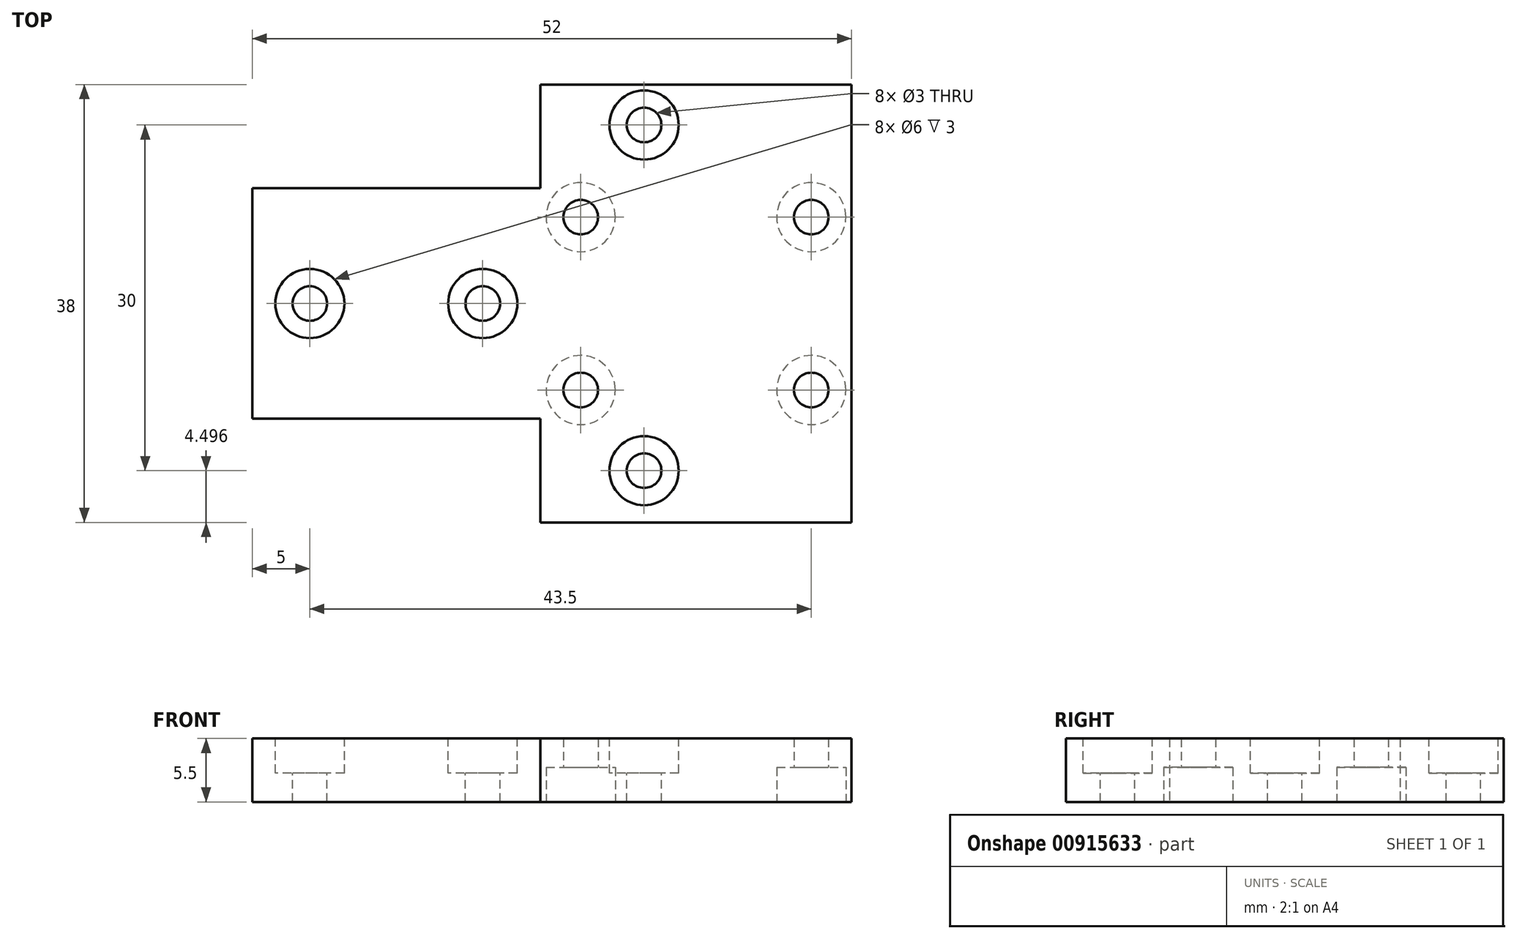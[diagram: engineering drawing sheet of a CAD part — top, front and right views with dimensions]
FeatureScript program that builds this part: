
annotation { "Feature Type Name" : "Feature", "Feature Type Description" : "" }
export const myFeature = defineFeature(function(context is Context, id is Id, definition is map)
    precondition{}
    {
        {
            var Q0;
            Q0=qCreatedBy(makeId("Top.planeOp"),FACE);
            var sketch = newSketch(context, id + "F0", { "sketchPlane" : qUnion([Q0])});
            skLineSegment(sketch, "E0.bottom", {"start": v(13.5, -19) * mm, "end": v(-13.5, -19) * mm});
            skLineSegment(sketch, "E0.top", {"start": v(13.5, 19) * mm, "end": v(-13.5, 19) * mm});
            skLineSegment(sketch, "E0.left", {"start": v(13.5, -19) * mm, "end": v(13.5, 19) * mm});
            skLineSegment(sketch, "E0.right", {"start": v(-13.5, -19) * mm, "end": v(-13.5, 19) * mm});
            skPoint(sketch, "E0.middle", {"position": v(0, 0) * mm});
            skLineSegment(sketch, "E1.bottom", {"start": v(10, -7.5) * mm, "end": v(-10, -7.5) * mm});
            skLineSegment(sketch, "E1.top", {"start": v(10, 7.5) * mm, "end": v(-10, 7.5) * mm});
            skLineSegment(sketch, "E1.left", {"start": v(10, -7.5) * mm, "end": v(10, 7.5) * mm});
            skLineSegment(sketch, "E1.right", {"start": v(-10, -7.5) * mm, "end": v(-10, 7.5) * mm});
            skSolve(sketch);
        }
        {
            var Q0;
            Q0=makeQuery(id+"F0.imprint","IMPRINT",FACE,{"disambiguationData":[TD([[makeQuery(id+"F0.imprint","IMPRINT",EDGE,{"derivedFrom":sQuery(id+"F0.wireOp",EDGE,"E0.bottom")}),-1.0]])]});
            var Q1;
            Q1=makeQuery(id+"F0.imprint","IMPRINT",FACE,{"disambiguationData":[TD([[makeQuery(id+"F0.imprint","IMPRINT",EDGE,{"derivedFrom":sQuery(id+"F0.wireOp",EDGE,"E1.bottom")}),-1.0]])]});
            extrude(context, id + "F1", {"entities" : qUnion([Q0, Q1]), "depth" : 5.5 * mm, "offsetDistance" : 25 * mm});
        }
        {
            var Q0;
            Q0=sQuery(id+"F0.wireOp",VERTEX,"E1.bottom.end");
            var Q1;
            Q1=sQuery(id+"F0.wireOp",VERTEX,"E1.top.end");
            var Q2;
            Q2=sQuery(id+"F0.wireOp",VERTEX,"E1.bottom.start");
            var Q3;
            Q3=sQuery(id+"F0.wireOp",VERTEX,"E1.top.start");
            var Q4;
            Q4=makeQuery(id+"F1.opExtrude","SWEPT_BODY",BODY,{"disambiguationData":[OSD([sQuery(id+"F0.wireOp",EDGE,"E0.bottom"),sQuery(id+"F0.wireOp",EDGE,"E0.top"),sQuery(id+"F0.wireOp",EDGE,"E0.left"),sQuery(id+"F0.wireOp",EDGE,"E0.right")])]});
            hole(context, id + "F2", {"style" : HoleStyle.C_BORE, "endStyle" : HoleEndStyle.BLIND, "oppositeDirection" : true, "holeDiameter" : 3 * mm, "cBoreDiameter" : 6 * mm, "cBoreDepth" : 3 * mm, "majorDiameter" : 5 * mm, "holeDepth" : 50 * mm, "isTappedThrough" : true, "tappedDepth" : 12 * mm, "tapClearance" : 3, "locations" : qUnion([Q0, Q1, Q2, Q3]), "scope" : qUnion([Q4])});
        }
        {
            var Q0;
            Q0=makeQuery(id+"F1.opExtrude","CAP_FACE",FACE,{"disambiguationData":[OSD([sQuery(id+"F0.wireOp",EDGE,"E0.bottom"),sQuery(id+"F0.wireOp",EDGE,"E0.top"),sQuery(id+"F0.wireOp",EDGE,"E0.left"),sQuery(id+"F0.wireOp",EDGE,"E0.right")])],"isStart":false});
            var sketch = newSketch(context, id + "F3", { "sketchPlane" : qUnion([Q0])});
            skLineSegment(sketch, "E2.bottom", {"start": v(-4.5, -14.5) * mm, "end": v(-13.5, -14.5) * mm});
            skLineSegment(sketch, "E2.top", {"start": v(-4.5, 15.5) * mm, "end": v(-13.5, 15.5) * mm});
            skLineSegment(sketch, "E2.left", {"start": v(-4.5, -14.5) * mm, "end": v(-4.5, 15.5) * mm});
            skLineSegment(sketch, "E2.right", {"start": v(-13.5, -14.5) * mm, "end": v(-13.5, 15.5) * mm});
            skPoint(sketch, "E2.middle", {"position": v(0, 0.5) * mm});
            skCircle(sketch, "E3", {"center": v(-4.5, -14.5) * mm, "radius": 7 * mm});
            skCircle(sketch, "E4", {"center": v(-4.5, 15.5) * mm, "radius": 7 * mm});
            skLineSegment(sketch, "E5", {"start": v(-13.5, 0) * mm, "end": v(-13.5, 10) * mm});
            skLineSegment(sketch, "E6", {"start": v(-13.5, 0) * mm, "end": v(-13.5, -10) * mm});
            skSolve(sketch);
        }
        {
            var Q0;
            Q0=sQuery(id+"F3.wireOp",VERTEX,"E2.bottom.start");
            var Q1;
            Q1=sQuery(id+"F3.wireOp",VERTEX,"E2.top.start");
            var Q2;
            Q2=makeQuery(id+"F1.opExtrude","SWEPT_BODY",BODY,{"disambiguationData":[OSD([sQuery(id+"F0.wireOp",EDGE,"E0.bottom"),sQuery(id+"F0.wireOp",EDGE,"E0.top"),sQuery(id+"F0.wireOp",EDGE,"E0.left"),sQuery(id+"F0.wireOp",EDGE,"E0.right")])]});
            hole(context, id + "F4", {"style" : HoleStyle.C_BORE, "endStyle" : HoleEndStyle.BLIND, "holeDiameter" : 3 * mm, "cBoreDiameter" : 6 * mm, "cBoreDepth" : 3 * mm, "majorDiameter" : 5 * mm, "holeDepth" : 50 * mm, "isTappedThrough" : true, "tappedDepth" : 12 * mm, "tapClearance" : 3, "locations" : qUnion([Q0, Q1]), "scope" : qUnion([Q2])});
        }
        {
            var Q0;
            Q0=makeQuery(id+"F1.opExtrude","SWEPT_FACE",FACE,{"disambiguationData":[OSD([sQuery(id+"F0.wireOp",EDGE,"E0.right")])]});
            var sketch = newSketch(context, id + "F5", { "sketchPlane" : qUnion([Q0])});
            skLineSegment(sketch, "E7.bottom", {"start": v(-10, 5.5) * mm, "end": v(10, 5.5) * mm});
            skLineSegment(sketch, "E7.top", {"start": v(-10, 0) * mm, "end": v(10, 0) * mm});
            skLineSegment(sketch, "E7.left", {"start": v(-10, 5.5) * mm, "end": v(-10, 0) * mm});
            skLineSegment(sketch, "E7.right", {"start": v(10, 5.5) * mm, "end": v(10, 0) * mm});
            skPoint(sketch, "E7.middle", {"position": v(0, 2.75) * mm});
            skPoint(sketch, "E7.middle.positionSnap0", {"position": v(0, 5.5) * mm});
            skPoint(sketch, "E7.middle.positionSnap1", {"position": v(19, 2.75) * mm});
            skPoint(sketch, "E7.centerSnap0", {"position": v(0, 5.5) * mm});
            skPoint(sketch, "E7.centerSnap1", {"position": v(19, 2.75) * mm});
            skSolve(sketch);
        }
        {
            var Q0;
            Q0=makeQuery(id+"F5.imprint","IMPRINT",FACE,{"disambiguationData":[TD([[makeQuery(id+"F5.imprint","IMPRINT",EDGE,{"derivedFrom":sQuery(id+"F5.wireOp",EDGE,"E7.bottom")}),1.0]])]});
            extrude(context, id + "F6", {"entities" : qUnion([Q0]), "operationType" : NewBodyOperationType.ADD, "depth" : 25 * mm, "offsetDistance" : 25 * mm});
        }
        {
            var Q0;
            Q0=makeQuery(id+"F6.boolean.opBoolean","MERGE",FACE,{"derivedFrom":[makeQuery(id+"F1.opExtrude","CAP_FACE",FACE,{"disambiguationData":[OSD([sQuery(id+"F0.wireOp",EDGE,"E0.bottom"),sQuery(id+"F0.wireOp",EDGE,"E0.top"),sQuery(id+"F0.wireOp",EDGE,"E0.left"),sQuery(id+"F0.wireOp",EDGE,"E0.right")])],"isStart":false}),makeQuery(id+"F6.opExtrude","SWEPT_FACE",FACE,{"disambiguationData":[OSD([sQuery(id+"F5.wireOp",EDGE,"E7.bottom")])]})]});
            var sketch = newSketch(context, id + "F7", { "sketchPlane" : qUnion([Q0])});
            skLineSegment(sketch, "E8", {"start": v(-38.5, 0) * mm, "end": v(-33.5, 0) * mm});
            skLineSegment(sketch, "E9", {"start": v(-33.5, 0) * mm, "end": v(-18.5, 0) * mm});
            skSolve(sketch);
        }
        {
            var Q0;
            Q0=sQuery(id+"F7.wireOp",VERTEX,"E8.end");
            var Q1;
            Q1=sQuery(id+"F7.wireOp",VERTEX,"E9.end");
            var Q2;
            Q2=makeQuery(id+"F1.opExtrude","SWEPT_BODY",BODY,{"disambiguationData":[OSD([sQuery(id+"F0.wireOp",EDGE,"E0.bottom"),sQuery(id+"F0.wireOp",EDGE,"E0.top"),sQuery(id+"F0.wireOp",EDGE,"E0.left"),sQuery(id+"F0.wireOp",EDGE,"E0.right")])]});
            hole(context, id + "F8", {"style" : HoleStyle.C_BORE, "endStyle" : HoleEndStyle.BLIND, "holeDiameter" : 3 * mm, "cBoreDiameter" : 6 * mm, "cBoreDepth" : 3 * mm, "majorDiameter" : 5 * mm, "holeDepth" : 50 * mm, "isTappedThrough" : true, "tappedDepth" : 12 * mm, "tapClearance" : 3, "locations" : qUnion([Q0, Q1]), "scope" : qUnion([Q2])});
        }
    });
